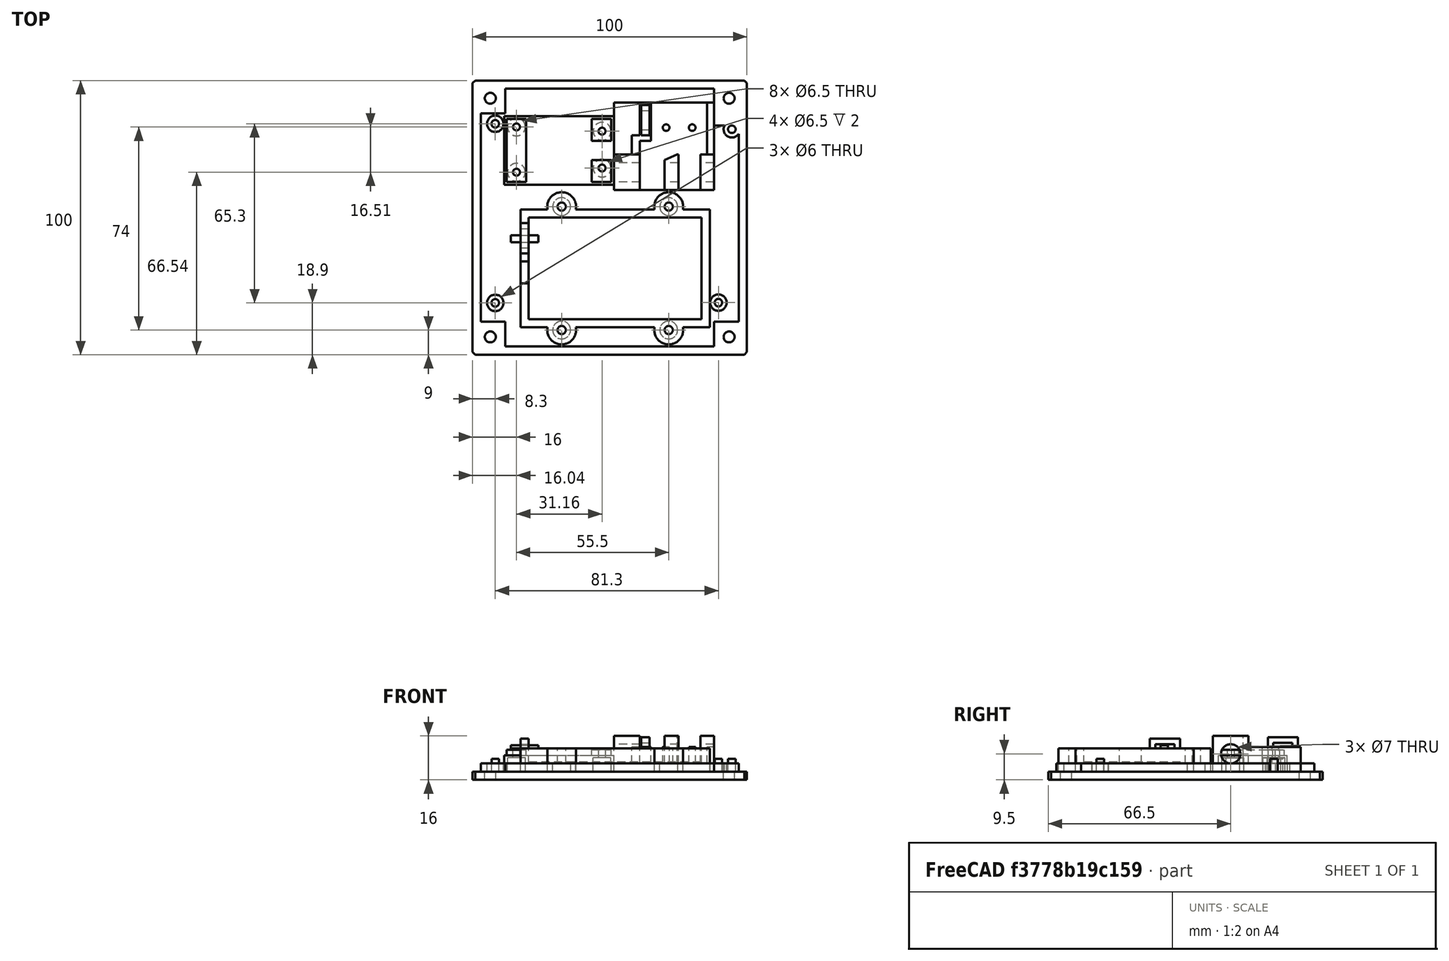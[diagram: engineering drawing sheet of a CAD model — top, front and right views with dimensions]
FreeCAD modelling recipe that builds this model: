
FCSTD DOCUMENT  (FreeCAD 0.19R)
Label: FullPowerModuleAssembly
License: All rights reserved
LicenseURL: http://en.wikipedia.org/wiki/All_rights_reserved
objects: Part::Cylinder×51, Part::Box×32, Part::MultiFuse×29, Part::Cut×15, Part::Chamfer×2
note: 129 computed .brp shape members not serialized (recipe doc carries the construction recipe); baked Part::Feature solids carry a one-line shape summary decoded from their .brp

FEATURE [Part::Box] Box  label="Mounting Plate Base"
  AttacherType = Attacher::AttachEngine3D
  Height = 3
  Length = 100
  Width = 100
FEATURE [Part::Cylinder] Cylinder  label="1U Post Holes"
  Angle = 360
  AttacherType = Attacher::AttachEngine3D
  Height = 3
  Placement = pos=(6.5,6.5,0) rot=(0,0,1;0rad)
  Radius = 2
FEATURE [Part::Cylinder] Cylinder001  label="1U Post Holes001"
  Angle = 360
  AttacherType = Attacher::AttachEngine3D
  Height = 3
  Placement = pos=(93.5,6.5,0) rot=(0,0,1;0rad)
  Radius = 2
FEATURE [Part::Cylinder] Cylinder002  label="1U Post Holes002"
  Angle = 360
  AttacherType = Attacher::AttachEngine3D
  Height = 3
  Placement = pos=(93.5,93.5,0) rot=(0,0,1;0rad)
  Radius = 2
FEATURE [Part::Cylinder] Cylinder003  label="1U Post Holes003"
  Angle = 360
  AttacherType = Attacher::AttachEngine3D
  Height = 3
  Placement = pos=(6.5,93.5,0) rot=(0,0,1;0rad)
  Radius = 2
FEATURE [Part::MultiFuse] Fusion  label="1U post holes assembly"
  Shapes = -> [Cylinder003,Cylinder,Cylinder001,Cylinder002]
FEATURE [Part::Cut] Cut
  Base = -> Box
  Tool = -> Fusion
FEATURE [Part::Cylinder] Cylinder004  label="Main ATA Board Mounting Screws"
  Angle = 360
  AttacherType = Attacher::AttachEngine3D
  Height = 4.7
  Placement = pos=(8.3,18.9,3) rot=(0,0,1;0rad)
  Radius = 1.375
FEATURE [Part::Cylinder] Cylinder005  label="Main ATA Board Mounting Screws001"
  Angle = 360
  AttacherType = Attacher::AttachEngine3D
  Height = 4.7
  Placement = pos=(8.3,84.2,3) rot=(0,0,1;0rad)
  Radius = 1.375
FEATURE [Part::Cylinder] Cylinder006  label="Main ATA Board Mounting Screws002"
  Angle = 360
  AttacherType = Attacher::AttachEngine3D
  Height = 4.7
  Placement = pos=(89.6,19,3) rot=(0,0,1;0rad)
  Radius = 1.375
FEATURE [Part::Cylinder] Cylinder007  label="Main ATA Board Mounting Screws003"
  Angle = 360
  AttacherType = Attacher::AttachEngine3D
  Height = 4.7
  Placement = pos=(94.5,82.2,3) rot=(0,0,1;0rad)
  Radius = 1.375
FEATURE [Part::MultiFuse] Fusion001  label="ATA Board mounting screw stubs"
  Shapes = -> [Cylinder007,Cylinder004,Cylinder005,Cylinder006]
FEATURE [Part::Chamfer] Chamfer
  Base = -> Cut
  Edges = 4 edges r=1: [Edge1,Edge3,Edge6,Edge15]
FEATURE [Part::MultiFuse] Fusion002  label="Mounting ATA Aluminium"
  Placement = pos=(0,0,-3) rot=(0,0,1;0rad)
  Shapes = -> [Chamfer,Fusion001]
FEATURE [Part::Box] Box001  label="Cube"
  AttacherType = Attacher::AttachEngine3D
  Height = 3
  Length = 94
  Placement = pos=(3,3,0) rot=(0,0,1;0rad)
  Width = 94
FEATURE [Part::Box] Box002  label="Cube001"
  AttacherType = Attacher::AttachEngine3D
  Height = 3
  Length = 12
  Width = 12
FEATURE [Part::Box] Box003  label="Cube002"
  AttacherType = Attacher::AttachEngine3D
  Height = 3
  Length = 12
  Placement = pos=(88,0,0) rot=(0,0,1;0rad)
  Width = 12
FEATURE [Part::Box] Box004  label="Cube003"
  AttacherType = Attacher::AttachEngine3D
  Height = 3
  Length = 12
  Placement = pos=(88,88,0) rot=(0,0,1;0rad)
  Width = 12
FEATURE [Part::Box] Box005  label="Cube004"
  AttacherType = Attacher::AttachEngine3D
  Height = 3
  Length = 12
  Placement = pos=(0,88,0) rot=(0,0,1;0rad)
  Width = 12
FEATURE [Part::MultiFuse] Fusion003
  Shapes = -> [Box002,Box003,Box004,Box005]
FEATURE [Part::Cut] Cut001
  Base = -> Box001
  Tool = -> Fusion003
FEATURE [Part::Cylinder] Cylinder008  label="Main ATA Board Mounting Screws004"
  Angle = 360
  AttacherType = Attacher::AttachEngine3D
  Height = 3
  Placement = pos=(8.3,18.9,0) rot=(0,0,1;0rad)
  Radius = 3
FEATURE [Part::Cylinder] Cylinder009  label="Main ATA Board Mounting Screws005"
  Angle = 360
  AttacherType = Attacher::AttachEngine3D
  Height = 3
  Placement = pos=(8.3,84.2,0) rot=(0,0,1;0rad)
  Radius = 3
FEATURE [Part::Cylinder] Cylinder010  label="Main ATA Board Mounting Screws006"
  Angle = 360
  AttacherType = Attacher::AttachEngine3D
  Height = 3
  Placement = pos=(89.6,19,0) rot=(0,0,1;0rad)
  Radius = 3
FEATURE [Part::Cylinder] Cylinder011  label="Main ATA Board Mounting Screws007"
  Angle = 360
  AttacherType = Attacher::AttachEngine3D
  Height = 3
  Placement = pos=(94.5,82.2,0) rot=(0,0,1;0rad)
  Radius = 3
FEATURE [Part::MultiFuse] Fusion004  label="ATA Board mounting screwholes"
  Shapes = -> [Cylinder011,Cylinder008,Cylinder009,Cylinder010]
FEATURE [Part::Cut] Cut002
  Base = -> Cut001
  Tool = -> Fusion004
FEATURE [Part::Box] Box006  label="Cube005"
  AttacherType = Attacher::AttachEngine3D
  Height = 3
  Length = 10
  Placement = pos=(88,83.5,0) rot=(0,0,1;0rad)
  Width = 10
FEATURE [Part::Cut] Cut003  label="Holed Backplate"
  Base = -> Cut002
  Tool = -> Box006
FEATURE [Part::Box] Box007  label="Cube006"
  AttacherType = Attacher::AttachEngine3D
  Height = 6
  Length = 63
  Width = 37
FEATURE [Part::Box] Box008  label="Cube007"
  AttacherType = Attacher::AttachEngine3D
  Height = 6
  Length = 10
  Placement = pos=(63,16,0) rot=(0,0,1;0rad)
  Width = 8
FEATURE [Part::MultiFuse] Fusion010  label="Battery Model"
  Placement = pos=(3,3,3) rot=(0,0,1;0rad)
  Shapes = -> [Box008,Box007]
FEATURE [Part::Box] Box009  label="Cube008"
  AttacherType = Attacher::AttachEngine3D
  Height = 8.5
  Length = 69
  Width = 43
FEATURE [Part::Cut] Cut010
  Base = -> Box009
  Tool = -> Fusion010
FEATURE [Part::Cylinder] Cylinder012
  Angle = 360
  AttacherType = Attacher::AttachEngine3D
  Height = 8.5
  Placement = pos=(15,-1,0) rot=(0,0,1;0rad)
  Radius = 5.25
FEATURE [Part::Cylinder] Cylinder013  label="Screw Shaft"
  Angle = 360
  AttacherType = Attacher::AttachEngine3D
  Height = 8.5
  Placement = pos=(15,-1,0) rot=(0,0,1;0rad)
  Radius = 1.5
FEATURE [Part::Cylinder] Cylinder014  label="Nut Recess"
  Angle = 360
  AttacherType = Attacher::AttachEngine3D
  Height = 3
  Placement = pos=(15,-1,0) rot=(0,0,1;0rad)
  Radius = 3.25
FEATURE [Part::MultiFuse] Fusion005  label="Base Bolt Assembly"
  Shapes = -> [Cylinder013,Cylinder014]
FEATURE [Part::Cut] Cut009  label="Base Bolt Flange - LL"
  Base = -> Cylinder012
  Tool = -> Fusion005
FEATURE [Part::Cylinder] Cylinder015  label="Screw Shaft001"
  Angle = 360
  AttacherType = Attacher::AttachEngine3D
  Height = 8.5
  Placement = pos=(15,-1,0) rot=(0,0,1;0rad)
  Radius = 1.5
FEATURE [Part::Cylinder] Cylinder016  label="Nut Recess001"
  Angle = 360
  AttacherType = Attacher::AttachEngine3D
  Height = 3
  Placement = pos=(15,-1,0) rot=(0,0,1;0rad)
  Radius = 3.25
FEATURE [Part::MultiFuse] Fusion006  label="Base Bolt Assembly001"
  Shapes = -> [Cylinder015,Cylinder016]
FEATURE [Part::Cylinder] Cylinder017
  Angle = 360
  AttacherType = Attacher::AttachEngine3D
  Height = 8.5
  Placement = pos=(15,-1,0) rot=(0,0,1;0rad)
  Radius = 5.25
FEATURE [Part::Cut] Cut004  label="Base Bolt Flange - LR"
  Base = -> Cylinder017
  Placement = pos=(39,0,0) rot=(0,0,1;0rad)
  Tool = -> Fusion006
FEATURE [Part::Cylinder] Cylinder018  label="Nut Recess002"
  Angle = 360
  AttacherType = Attacher::AttachEngine3D
  Height = 3
  Placement = pos=(15,-1,0) rot=(0,0,1;0rad)
  Radius = 3.25
FEATURE [Part::Cylinder] Cylinder019  label="Screw Shaft002"
  Angle = 360
  AttacherType = Attacher::AttachEngine3D
  Height = 8.5
  Placement = pos=(15,-1,0) rot=(0,0,1;0rad)
  Radius = 1.5
FEATURE [Part::MultiFuse] Fusion007  label="Base Bolt Assembly002"
  Shapes = -> [Cylinder019,Cylinder018]
FEATURE [Part::Cylinder] Cylinder020
  Angle = 360
  AttacherType = Attacher::AttachEngine3D
  Height = 8.5
  Placement = pos=(15,-1,0) rot=(0,0,1;0rad)
  Radius = 5.25
FEATURE [Part::Cut] Cut005  label="Base Bolt Flange - UR"
  Base = -> Cylinder020
  Placement = pos=(39,45,0) rot=(0,0,1;0rad)
  Tool = -> Fusion007
FEATURE [Part::Cylinder] Cylinder021
  Angle = 360
  AttacherType = Attacher::AttachEngine3D
  Height = 8.5
  Placement = pos=(15,-1,0) rot=(0,0,1;0rad)
  Radius = 5.25
FEATURE [Part::Cylinder] Cylinder022  label="Screw Shaft003"
  Angle = 360
  AttacherType = Attacher::AttachEngine3D
  Height = 8.5
  Placement = pos=(15,-1,0) rot=(0,0,1;0rad)
  Radius = 1.5
FEATURE [Part::Cylinder] Cylinder023  label="Nut Recess003"
  Angle = 360
  AttacherType = Attacher::AttachEngine3D
  Height = 3
  Placement = pos=(15,-1,0) rot=(0,0,1;0rad)
  Radius = 3.25
FEATURE [Part::MultiFuse] Fusion008  label="Base Bolt Assembly003"
  Shapes = -> [Cylinder022,Cylinder023]
FEATURE [Part::Cut] Cut006  label="Base Bolt Flange - UL"
  Base = -> Cylinder021
  Placement = pos=(0,45,0) rot=(0,0,1;0rad)
  Tool = -> Fusion008
FEATURE [Part::Cylinder] Cylinder024  label="Screw Shaft004"
  Angle = 360
  AttacherType = Attacher::AttachEngine3D
  Height = 8.5
  Placement = pos=(15,-1,0) rot=(0,0,1;0rad)
  Radius = 1.5
FEATURE [Part::Cylinder] Cylinder025  label="Nut Recess004"
  Angle = 360
  AttacherType = Attacher::AttachEngine3D
  Height = 3
  Placement = pos=(15,-1,0) rot=(0,0,1;0rad)
  Radius = 3.25
FEATURE [Part::MultiFuse] Fusion009  label="Base Bolt Assembly - LL"
  Shapes = -> [Cylinder024,Cylinder025]
FEATURE [Part::Cylinder] Cylinder026  label="Screw Shaft005"
  Angle = 360
  AttacherType = Attacher::AttachEngine3D
  Height = 8.5
  Placement = pos=(15,-1,0) rot=(0,0,1;0rad)
  Radius = 1.5
FEATURE [Part::Cylinder] Cylinder027  label="Nut Recess005"
  Angle = 360
  AttacherType = Attacher::AttachEngine3D
  Height = 3
  Placement = pos=(15,-1,0) rot=(0,0,1;0rad)
  Radius = 3.25
FEATURE [Part::MultiFuse] Fusion011  label="Base Bolt Assembly - LR"
  Placement = pos=(39,0,0) rot=(0,0,1;0rad)
  Shapes = -> [Cylinder026,Cylinder027]
FEATURE [Part::Cylinder] Cylinder028  label="Nut Recess006"
  Angle = 360
  AttacherType = Attacher::AttachEngine3D
  Height = 3
  Placement = pos=(15,-1,0) rot=(0,0,1;0rad)
  Radius = 3.25
FEATURE [Part::Cylinder] Cylinder029  label="Screw Shaft006"
  Angle = 360
  AttacherType = Attacher::AttachEngine3D
  Height = 8.5
  Placement = pos=(15,-1,0) rot=(0,0,1;0rad)
  Radius = 1.5
FEATURE [Part::MultiFuse] Fusion012  label="Base Bolt Assembly - UR"
  Placement = pos=(39,45,0) rot=(0,0,1;0rad)
  Shapes = -> [Cylinder029,Cylinder028]
FEATURE [Part::Cylinder] Cylinder030  label="Screw Shaft007"
  Angle = 360
  AttacherType = Attacher::AttachEngine3D
  Height = 8.5
  Placement = pos=(15,-1,0) rot=(0,0,1;0rad)
  Radius = 1.5
FEATURE [Part::Cylinder] Cylinder031  label="Nut Recess007"
  Angle = 360
  AttacherType = Attacher::AttachEngine3D
  Height = 3
  Placement = pos=(15,-1,0) rot=(0,0,1;0rad)
  Radius = 3.25
FEATURE [Part::MultiFuse] Fusion013  label="Base Bolt Assembly - UL"
  Placement = pos=(0,45,0) rot=(0,0,1;0rad)
  Shapes = -> [Cylinder030,Cylinder031]
FEATURE [Part::MultiFuse] Fusion014  label="Base Bolt Remove Assembly"
  Shapes = -> [Fusion013,Fusion009,Fusion011,Fusion012]
FEATURE [Part::Cut] Cut007
  Base = -> Cut010
  Tool = -> Fusion014
FEATURE [Part::MultiFuse] Fusion015  label="Base Bolt Assemblies"
  Shapes = -> [Cut006,Cut005,Cut004,Cut009]
FEATURE [Part::Box] Box010  label="Cube009"
  AttacherType = Attacher::AttachEngine3D
  Height = 5.5
  Length = 10
  Placement = pos=(63,16,0) rot=(0,0,1;0rad)
  Width = 8
FEATURE [Part::Box] Box011  label="Cube010"
  AttacherType = Attacher::AttachEngine3D
  Height = 5.5
  Length = 63
  Width = 37
FEATURE [Part::MultiFuse] Fusion016  label="Battery Model002"
  Placement = pos=(3,3,3) rot=(0,0,1;0rad)
  Shapes = -> [Box010,Box011]
FEATURE [Part::Cut] Cut008  label="Base Bolt Assemblies - no Bat"
  Base = -> Fusion015
  Tool = -> Fusion016
FEATURE [Part::MultiFuse] Fusion017  label="Battery Backside"
  Placement = pos=(86.5,53,0) rot=(0,0,1;3.14159rad)
  Shapes = -> [Cut007,Cut008]
FEATURE [Part::Box] Box012  label="Base Plate"
  AttacherType = Attacher::AttachEngine3D
  Height = 3
  Length = 40
  Width = 32
FEATURE [Part::Box] Box013  label="Pin Block 1"
  AttacherType = Attacher::AttachEngine3D
  Height = 10
  Length = 5
  Placement = pos=(0,19,3) rot=(0,0,1;0rad)
  Width = 13
FEATURE [Part::Box] Box014  label="Pin Block 3"
  AttacherType = Attacher::AttachEngine3D
  Height = 10
  Length = 13
  Placement = pos=(27,19,3) rot=(0,0,1;0rad)
  Width = 13
FEATURE [Part::Box] Box015  label="Switch wall right"
  AttacherType = Attacher::AttachEngine3D
  Height = 6
  Length = 4
  Placement = pos=(23,0,3) rot=(0,0,1;0rad)
  Width = 14
FEATURE [Part::Box] Box016  label="Switch wall left"
  AttacherType = Attacher::AttachEngine3D
  Height = 6
  Length = 2.5
  Placement = pos=(0,0,3) rot=(0,0,1;0rad)
  Width = 19
FEATURE [Part::Cylinder] Cylinder032
  Angle = 360
  AttacherType = Attacher::AttachEngine3D
  Height = 6
  Placement = pos=(7.95,2.5,0) rot=(0,0,1;0rad)
  Radius = 1.2
FEATURE [Part::Cylinder] Cylinder033
  Angle = 360
  AttacherType = Attacher::AttachEngine3D
  Height = 6
  Placement = pos=(17.45,2.5,0) rot=(0,0,1;0rad)
  Radius = 1.2
FEATURE [Part::MultiFuse] Fusion019  label="Switch Pins"
  Placement = pos=(0,6.7,3) rot=(0,0,1;0rad)
  Shapes = -> [Cylinder032,Cylinder033]
FEATURE [Part::Cylinder] Cylinder034  label="Locking Pin Model"
  Angle = 360
  AttacherType = Attacher::AttachEngine3D
  Height = 40
  Placement = pos=(0,25.5,6.5) rot=(0,1,0;1.5708rad)
  Radius = 3.5
FEATURE [Part::Box] Box017  label="Dust cover block"
  AttacherType = Attacher::AttachEngine3D
  Height = 6
  Length = 3
  Placement = pos=(27,12,3) rot=(0,0,1;0rad)
  Width = 7
FEATURE [Part::Box] Box018  label="Pin Block 2"
  AttacherType = Attacher::AttachEngine3D
  Height = 10
  Length = 5
  Placement = pos=(13,19,3) rot=(0,0,1;0rad)
  Width = 13
FEATURE [Part::Chamfer] Chamfer001  label="Pin Block 2 - with arm cut"
  Base = -> Box018
  Edges = 1 edges: [Edge5 r1=2 r2=4.5]
FEATURE [Part::MultiFuse] Fusion018
  Shapes = -> [Chamfer001,Box013,Box014]
FEATURE [Part::Cut] Cut011  label="Pin Blocks Holed"
  Base = -> Fusion018
  Tool = -> Cylinder034
FEATURE [Part::MultiFuse] Fusion020  label="Power Pin Switch Frame"
  Placement = pos=(88,92,0) rot=(0,0,1;3.14159rad)
  Shapes = -> [Fusion019,Box016,Box015,Box012,Box017,Cut011]
FEATURE [Part::Box] Box019  label="Main Plate"
  AttacherType = Attacher::AttachEngine3D
  Height = 3
  Length = 40
  Placement = pos=(-1,-1,0) rot=(0,0,1;0rad)
  Width = 25
FEATURE [Part::Cylinder] Cylinder035
  Angle = 360
  AttacherType = Attacher::AttachEngine3D
  Height = 5
  Placement = pos=(2.54,19.05,0) rot=(0,0,1;0rad)
  Radius = 1.27
FEATURE [Part::Cylinder] Cylinder036
  Angle = 360
  AttacherType = Attacher::AttachEngine3D
  Height = 5
  Placement = pos=(2.54,2.54,0) rot=(0,0,1;0rad)
  Radius = 1.27
FEATURE [Part::Cylinder] Cylinder037
  Angle = 360
  AttacherType = Attacher::AttachEngine3D
  Height = 5
  Placement = pos=(33.7,17.5,0) rot=(0,0,1;0rad)
  Radius = 1.27
FEATURE [Part::Cylinder] Cylinder038
  Angle = 360
  AttacherType = Attacher::AttachEngine3D
  Height = 5
  Placement = pos=(33.7,4.064,0) rot=(0,0,1;0rad)
  Radius = 1.27
FEATURE [Part::MultiFuse] Fusion021  label="Screw Holes"
  Placement = pos=(1,1,0) rot=(0,0,1;0rad)
  Shapes = -> [Cylinder036,Cylinder035,Cylinder037,Cylinder038]
FEATURE [Part::Box] Box020  label="Cube011"
  AttacherType = Attacher::AttachEngine3D
  Height = 2
  Length = 7
  Placement = pos=(0,0,3) rot=(0,0,1;0rad)
  Width = 23
FEATURE [Part::Box] Box021  label="Cube012"
  AttacherType = Attacher::AttachEngine3D
  Height = 2
  Length = 7
  Placement = pos=(31,15,3) rot=(0,0,1;0rad)
  Width = 8
FEATURE [Part::Box] Box022  label="Cube013"
  AttacherType = Attacher::AttachEngine3D
  Height = 2
  Length = 7
  Placement = pos=(31,0,3) rot=(0,0,1;0rad)
  Width = 8
FEATURE [Part::Cylinder] Cylinder039
  Angle = 360
  AttacherType = Attacher::AttachEngine3D
  Height = 2
  Placement = pos=(3.54,20.05,0) rot=(0,0,1;0rad)
  Radius = 3.25
FEATURE [Part::Cylinder] Cylinder040
  Angle = 360
  AttacherType = Attacher::AttachEngine3D
  Height = 2
  Placement = pos=(3.54,3.54,0) rot=(0,0,1;0rad)
  Radius = 3.25
FEATURE [Part::MultiFuse] Fusion022  label="Standoff Blocks"
  Shapes = -> [Box020,Box021,Box022]
FEATURE [Part::Cylinder] Cylinder041
  Angle = 360
  AttacherType = Attacher::AttachEngine3D
  Height = 2
  Placement = pos=(34.7,18.5,0) rot=(0,0,1;0rad)
  Radius = 3.25
FEATURE [Part::Cylinder] Cylinder042
  Angle = 360
  AttacherType = Attacher::AttachEngine3D
  Height = 2
  Placement = pos=(34.7,5.06,0) rot=(0,0,1;0rad)
  Radius = 3.25
FEATURE [Part::MultiFuse] Fusion023  label="Washer Bolt Holes"
  Shapes = -> [Cylinder039,Cylinder040,Cylinder041,Cylinder042]
FEATURE [Part::MultiFuse] Fusion024  label="Complete Blackplate Holes"
  Shapes = -> [Fusion021,Fusion023]
FEATURE [Part::MultiFuse] Fusion025
  Shapes = -> [Box019,Fusion022]
FEATURE [Part::Cut] Cut012  label="Regulator Base"
  Base = -> Fusion025
  Placement = pos=(12.5,63,3) rot=(0,0,1;0rad)
  Tool = -> Fusion024
FEATURE [Part::Box] Box023  label="Cube014"
  AttacherType = Attacher::AttachEngine3D
  Height = 13
  Length = 3.5
  Placement = pos=(48,60,0) rot=(0,0,1;0rad)
  Width = 32
FEATURE [Part::Cut] Cut013  label="Switch Pin - fitted"
  Base = -> Fusion020
  Tool = -> Box023
FEATURE [Part::Cylinder] Cylinder044  label="Nut Recess - Baseplate 01"
  Angle = 360
  AttacherType = Attacher::AttachEngine3D
  Height = 3
  Placement = pos=(32.5,9,0) rot=(0,0,1;0rad)
  Radius = 3.25
FEATURE [Part::Cylinder] Cylinder045  label="Nut Recess - Baseplate 002"
  Angle = 360
  AttacherType = Attacher::AttachEngine3D
  Height = 3
  Placement = pos=(71.5,9,0) rot=(0,0,1;0rad)
  Radius = 3.25
FEATURE [Part::Cylinder] Cylinder046  label="Nut Recess - Baseplate 003"
  Angle = 360
  AttacherType = Attacher::AttachEngine3D
  Height = 3
  Placement = pos=(32.5,54,0) rot=(0,0,1;0rad)
  Radius = 3.25
FEATURE [Part::Cylinder] Cylinder047  label="Nut Recess - Baseplate 004"
  Angle = 360
  AttacherType = Attacher::AttachEngine3D
  Height = 3
  Placement = pos=(47.25,68,0) rot=(0,0,1;0rad)
  Radius = 3.25
FEATURE [Part::Cylinder] Cylinder048  label="Nut Recess - Baseplate 005"
  Angle = 360
  AttacherType = Attacher::AttachEngine3D
  Height = 3
  Placement = pos=(71.5,54,0) rot=(0,0,1;0rad)
  Radius = 3.25
FEATURE [Part::Cylinder] Cylinder049  label="Nut Recess - Baseplate 006"
  Angle = 360
  AttacherType = Attacher::AttachEngine3D
  Height = 3
  Placement = pos=(47.25,81.5,0) rot=(0,0,1;0rad)
  Radius = 3.25
FEATURE [Part::Cylinder] Cylinder050  label="Nut Recess - Baseplate 007"
  Angle = 360
  AttacherType = Attacher::AttachEngine3D
  Height = 3
  Placement = pos=(16,66.5,0) rot=(0,0,1;0rad)
  Radius = 3.25
FEATURE [Part::Cylinder] Cylinder051  label="Nut Recess - Baseplate 008"
  Angle = 360
  AttacherType = Attacher::AttachEngine3D
  Height = 3
  Placement = pos=(16,83,0) rot=(0,0,1;0rad)
  Radius = 3.25
FEATURE [Part::MultiFuse] Fusion026
  Shapes = -> [Cylinder051,Cylinder046,Cylinder044,Cylinder047,Cylinder050,Cylinder049,Cylinder045,Cylinder048]
FEATURE [Part::Cut] Cut014  label="Backplate - with nut recesses"
  Base = -> Cut003
  Tool = -> Fusion026
FEATURE [Part::Box] Box024  label="Ziptie"
  AttacherType = Attacher::AttachEngine3D
  Height = 1.1
  Length = 10
  Placement = pos=(14,41,8.5) rot=(0,0,1;0rad)
  Width = 2.6
FEATURE [Part::Box] Box025  label="Ziptie001"
  AttacherType = Attacher::AttachEngine3D
  Height = 2
  Length = 3
  Placement = pos=(17.5,39,10) rot=(0,0,1;0rad)
  Width = 7
FEATURE [Part::Box] Box026  label="Ziptie002"
  AttacherType = Attacher::AttachEngine3D
  Height = 3.5
  Length = 3
  Placement = pos=(17.5,37,8.5) rot=(0,0,1;0rad)
  Width = 2
FEATURE [Part::Box] Box027  label="Ziptie003"
  AttacherType = Attacher::AttachEngine3D
  Height = 3.5
  Length = 3
  Placement = pos=(17.5,46,8.5) rot=(0,0,1;0rad)
  Width = 2
FEATURE [Part::MultiFuse] Fusion027  label="Battery Ziptie Ring"
  Shapes = -> [Box026,Box025,Box027]
FEATURE [Part::Box] Box028  label="Ziptie004"
  AttacherType = Attacher::AttachEngine3D
  Height = 2
  Length = 3
  Placement = pos=(17.5,39,10) rot=(0,0,1;0rad)
  Width = 7
FEATURE [Part::Box] Box029  label="Ziptie005"
  AttacherType = Attacher::AttachEngine3D
  Height = 3.5
  Length = 3
  Placement = pos=(17.5,46,8.5) rot=(0,0,1;0rad)
  Width = 2
FEATURE [Part::Box] Box030  label="Ziptie006"
  AttacherType = Attacher::AttachEngine3D
  Height = 3.5
  Length = 3
  Placement = pos=(17.5,37,8.5) rot=(0,0,1;0rad)
  Width = 2
FEATURE [Part::MultiFuse] Fusion028  label="Main Power Ziptie Ring"
  Placement = pos=(44,43,0.5) rot=(0,0,1;0rad)
  Shapes = -> [Box030,Box028,Box029]
FEATURE [Part::Box] Box031  label="Cube015"
  AttacherType = Attacher::AttachEngine3D
  Height = 0.7
  Length = 63
  Placement = pos=(20.5,13,3) rot=(0,0,1;0rad)
  Width = 37
